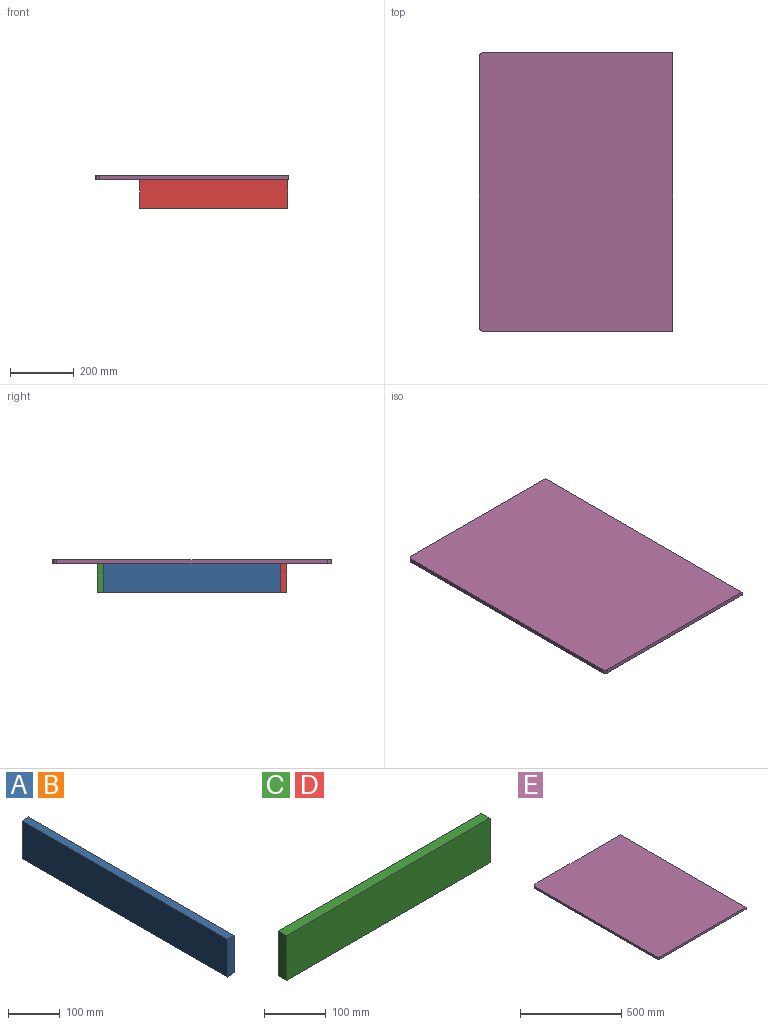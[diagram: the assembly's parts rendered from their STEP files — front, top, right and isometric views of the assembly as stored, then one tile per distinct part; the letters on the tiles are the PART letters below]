
ASSEMBLY  parts=5 mates=5
PART A: 6 faces, bbox 19.1x558.8x88.9 mm
  f0: plane 558.8x19.05mm, normal (0,0,-1), area 10645.1mm2, adj f1,f3,f4,f5
  f1: plane 88.9x19.05mm, normal (0,1,0), area 1693.5mm2, adj f0,f2,f3,f4
  f2: plane 558.8x19.05mm, normal (0,0,1), area 10645.1mm2, adj f1,f3,f4,f5
  f3: plane 558.8x88.9mm, normal (1,0,0), area 49677.3mm2, adj f0,f1,f2,f5
  f4: plane 558.8x88.9mm, normal (-1,0,0), area 49677.3mm2, adj f0,f1,f2,f5
  f5: plane 88.9x19.05mm, normal (0,-1,0), area 1693.5mm2, adj f0,f2,f3,f4
PART B: same geometry as A
PART C: 6 faces, bbox 466.8x19.1x88.9 mm
  f0: plane 88.9x19.05mm, normal (-1,0,0), area 1693.5mm2, adj f1,f3,f4,f5
  f1: plane 466.8x88.9mm, normal (0,-1,0), area 41498.6mm2, adj f0,f2,f4,f5
  f2: plane 88.9x19.05mm, normal (1,0,0), area 1693.5mm2, adj f1,f3,f4,f5
  f3: plane 466.8x88.9mm, normal (0,1,0), area 41498.6mm2, adj f0,f2,f4,f5
  f4: plane 466.8x19.05mm, normal (0,0,-1), area 8892.6mm2, adj f0,f1,f2,f3
  f5: plane 466.8x19.05mm, normal (0,0,1), area 8892.6mm2, adj f0,f1,f2,f3
PART D: same geometry as C
PART E: 8 faces, bbox 609.6x876.3x12.7 mm
  f0: plane 876.3x12.7mm, normal (1,0,0), area 11129mm2, adj f1,f3,f4,f5
  f1: plane 596.9x12.7mm, normal (0,1,0), area 7580.6mm2, adj f0,f4,f5,f6
  f2: plane 850.9x12.7mm, normal (-1,0,0), area 10806.4mm2, adj f4,f5,f6,f7
  f3: plane 596.9x12.7mm, normal (0,-1,0), area 7580.6mm2, adj f0,f4,f5,f7
  f4: plane 876.3x609.6mm, normal (0,0,1), area 534123.3mm2, adj f0,f1,f2,f3,f6,f7
  f5: plane 876.3x609.6mm, normal (0,0,-1), area 534123.3mm2, adj f0,f1,f2,f3,f6,f7
  f6: cylinder r=12.7mm len=12.7mm, axis (0,0,-1), area 253.4mm2, adj f1,f2,f4,f5
  f7: cylinder r=12.7mm len=12.7mm, axis (0,0,1), area 253.4mm2, adj f2,f3,f4,f5
PLACE A rot(axis=(1,0,0),180deg) t=(0,0,-88.9)mm
PLACE B t=(447.75,0,0)mm
PLACE C rot(axis=(0,1,0),180deg) t=(-473,0,-88.9)mm
PLACE D rot(axis=(1,0,0),180deg) t=(0,0,-88.9)mm
PLACE E at identity fixed
MATE fastened C.f4 <-> A.f0  axis (0,0,1) through (-469.9,279.4,0)mm
MATE fastened E.f5 <-> B.f2  axis (0,0,-1) through (0,0,0)mm
MATE fastened D.f5 <-> B.f0  axis (0,0,-1) through (-3.1,-279.4,-88.9)mm
MATE fastened A.f2 <-> C.f5  axis (0,0,-1) through (-469.9,279.4,-88.9)mm
MATE fastened A.f2 <-> D.f5  axis (0,0,-1) through (-469.9,-279.4,-88.9)mm
